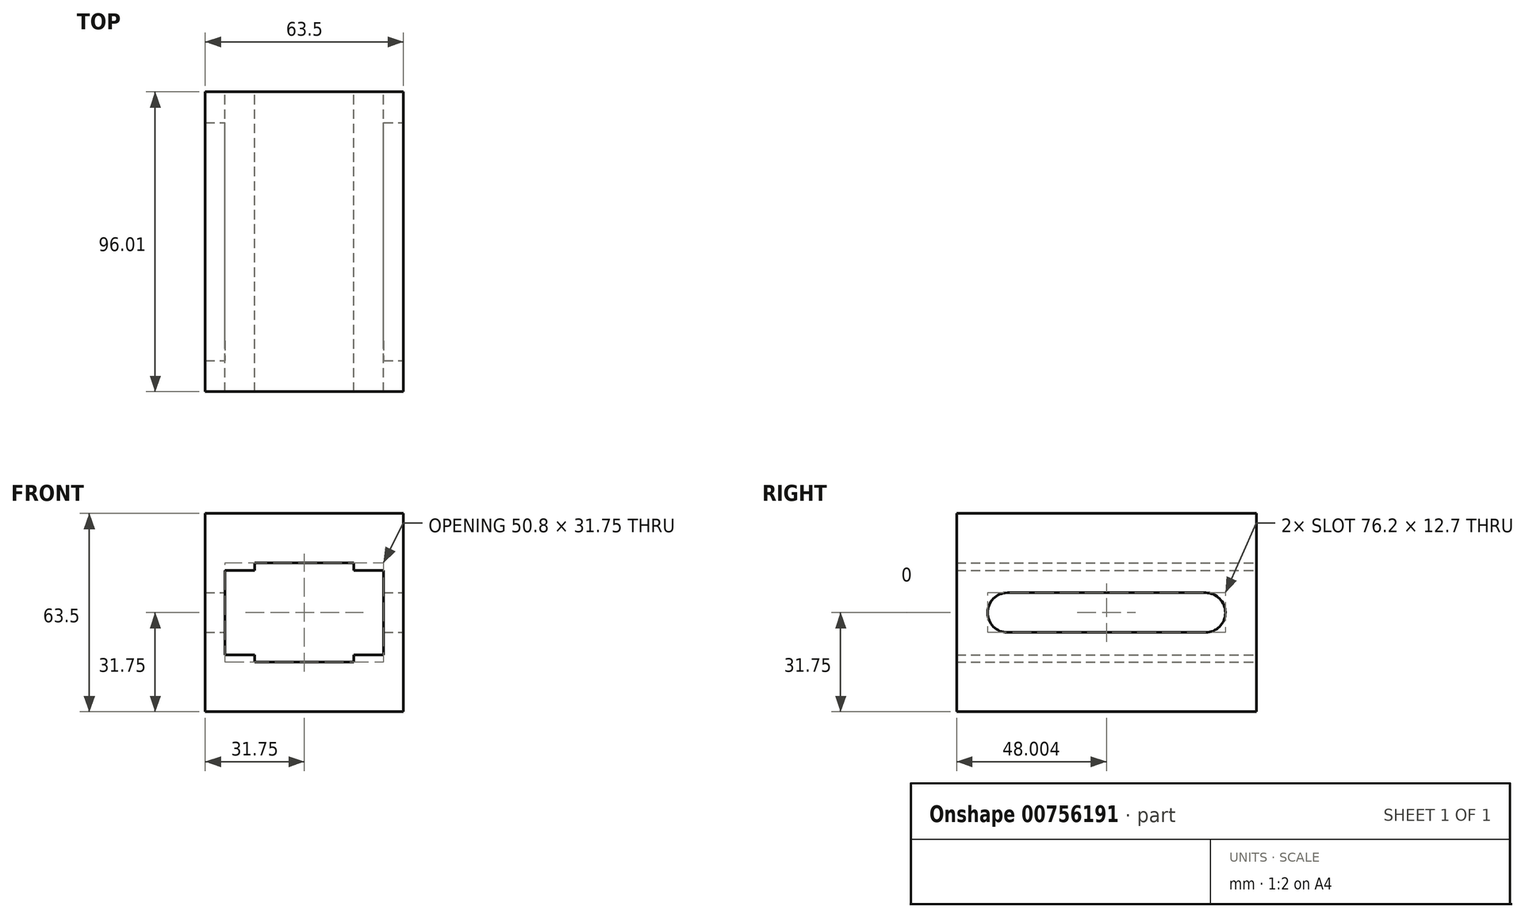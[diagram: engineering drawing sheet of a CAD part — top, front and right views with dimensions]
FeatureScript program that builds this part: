
annotation { "Feature Type Name" : "Feature", "Feature Type Description" : "" }
export const myFeature = defineFeature(function(context is Context, id is Id, definition is map)
    precondition{}
    {
        {
            var Q0;
            Q0=qCreatedBy(makeId("Front.planeOp"),FACE);
            var sketch = newSketch(context, id + "F0", { "sketchPlane" : qUnion([Q0])});
            skLineSegment(sketch, "E0.bottom", {"start": v(-31.75, 31.75) * mm, "end": v(31.75, 31.75) * mm});
            skLineSegment(sketch, "E0.left", {"start": v(-31.75, 31.75) * mm, "end": v(-31.75, -31.75) * mm});
            skLineSegment(sketch, "E0.right", {"start": v(31.75, 31.75) * mm, "end": v(31.75, -31.75) * mm});
            skLineSegment(sketch, "E1", {"start": v(-31.75, 31.75) * mm, "end": v(31.75, -31.75) * mm, "construction": true});
            skLineSegment(sketch, "E2", {"start": v(31.75, -31.75) * mm, "end": v(-31.75, -31.75) * mm});
            skPoint(sketch, "E3", {"position": v(0, 0) * mm});
            skLineSegment(sketch, "E4.bottom", {"start": v(15.87, 15.88) * mm, "end": v(-15.87, 15.87) * mm});
            skLineSegment(sketch, "E4.top", {"start": v(15.87, -15.87) * mm, "end": v(-15.87, -15.88) * mm});
            skLineSegment(sketch, "E4.left", {"start": v(25.4, 13.5) * mm, "end": v(25.4, -13.5) * mm});
            skLineSegment(sketch, "E4.right", {"start": v(-25.4, 13.5) * mm, "end": v(-25.4, -13.5) * mm});
            skLineSegment(sketch, "E5", {"start": v(-25.4, -13.5) * mm, "end": v(-15.87, -13.5) * mm});
            skLineSegment(sketch, "E6", {"start": v(-15.87, -13.5) * mm, "end": v(-15.87, -15.88) * mm});
            skLineSegment(sketch, "E7", {"start": v(-25.4, 13.5) * mm, "end": v(-15.88, 13.5) * mm});
            skLineSegment(sketch, "E8", {"start": v(-15.88, 13.5) * mm, "end": v(-15.88, 15.87) * mm});
            skLineSegment(sketch, "E9", {"start": v(15.87, 15.88) * mm, "end": v(15.87, 13.5) * mm});
            skLineSegment(sketch, "E10", {"start": v(15.87, 13.5) * mm, "end": v(25.4, 13.5) * mm});
            skLineSegment(sketch, "E11", {"start": v(15.87, -15.87) * mm, "end": v(15.87, -13.5) * mm});
            skLineSegment(sketch, "E12", {"start": v(15.88, -13.5) * mm, "end": v(25.4, -13.5) * mm});
            skPoint(sketch, "E13.orphan", {"position": v(-25.4, 15.87) * mm});
            skPoint(sketch, "E14.orphan", {"position": v(25.4, 15.88) * mm});
            skPoint(sketch, "E15.orphan", {"position": v(25.4, -15.87) * mm});
            skPoint(sketch, "E16.orphan", {"position": v(-25.4, -15.88) * mm});
            skSolve(sketch);
        }
        {
            var Q0;
            Q0 = qSketchRegion(id + "F0", true);
            extrude(context, id + "F1", {"entities" : qUnion([Q0]), "depth" : 96.01 * mm, "offsetDistance" : 25.4 * mm});
        }
        {
            var Q0;
            Q0=makeQuery(id+"F1.opExtrude","SWEPT_FACE",FACE,{"disambiguationData":[OSD([sQuery(id+"F0.wireOp",EDGE,"E0.right")])]});
            var sketch = newSketch(context, id + "F2", { "sketchPlane" : qUnion([Q0])});
            skLineSegment(sketch, "E17", {"start": v(-79.76, -6.35) * mm, "end": v(-16.26, -6.35) * mm});
            skArc(sketch, "E18", {"start": v(-16.26, -6.35) * mm, "mid": v(-9.9, 0) * mm, "end": v(-16.26, 6.35) * mm});
            skArc(sketch, "E19", {"start": v(-79.76, 6.35) * mm, "mid": v(-86.1, 0) * mm, "end": v(-79.76, -6.35) * mm});
            skLineSegment(sketch, "E20", {"start": v(-79.76, 6.35) * mm, "end": v(-16.26, 6.35) * mm});
            skLineSegment(sketch, "E21", {"start": v(0, 0) * mm, "end": v(-16.26, 0) * mm, "construction": true});
            skLineSegment(sketch, "E22", {"start": v(-79.76, 0) * mm, "end": v(-96.01, 0) * mm, "construction": true});
            skSolve(sketch);
        }
        {
            var Q0;
            Q0 = qSketchRegion(id + "F2", true);
            extrude(context, id + "F3", {"entities" : qUnion([Q0]), "operationType" : NewBodyOperationType.REMOVE, "oppositeDirection" : true, "depth" : 73.9 * mm, "offsetDistance" : 25.4 * mm});
        }
    });
